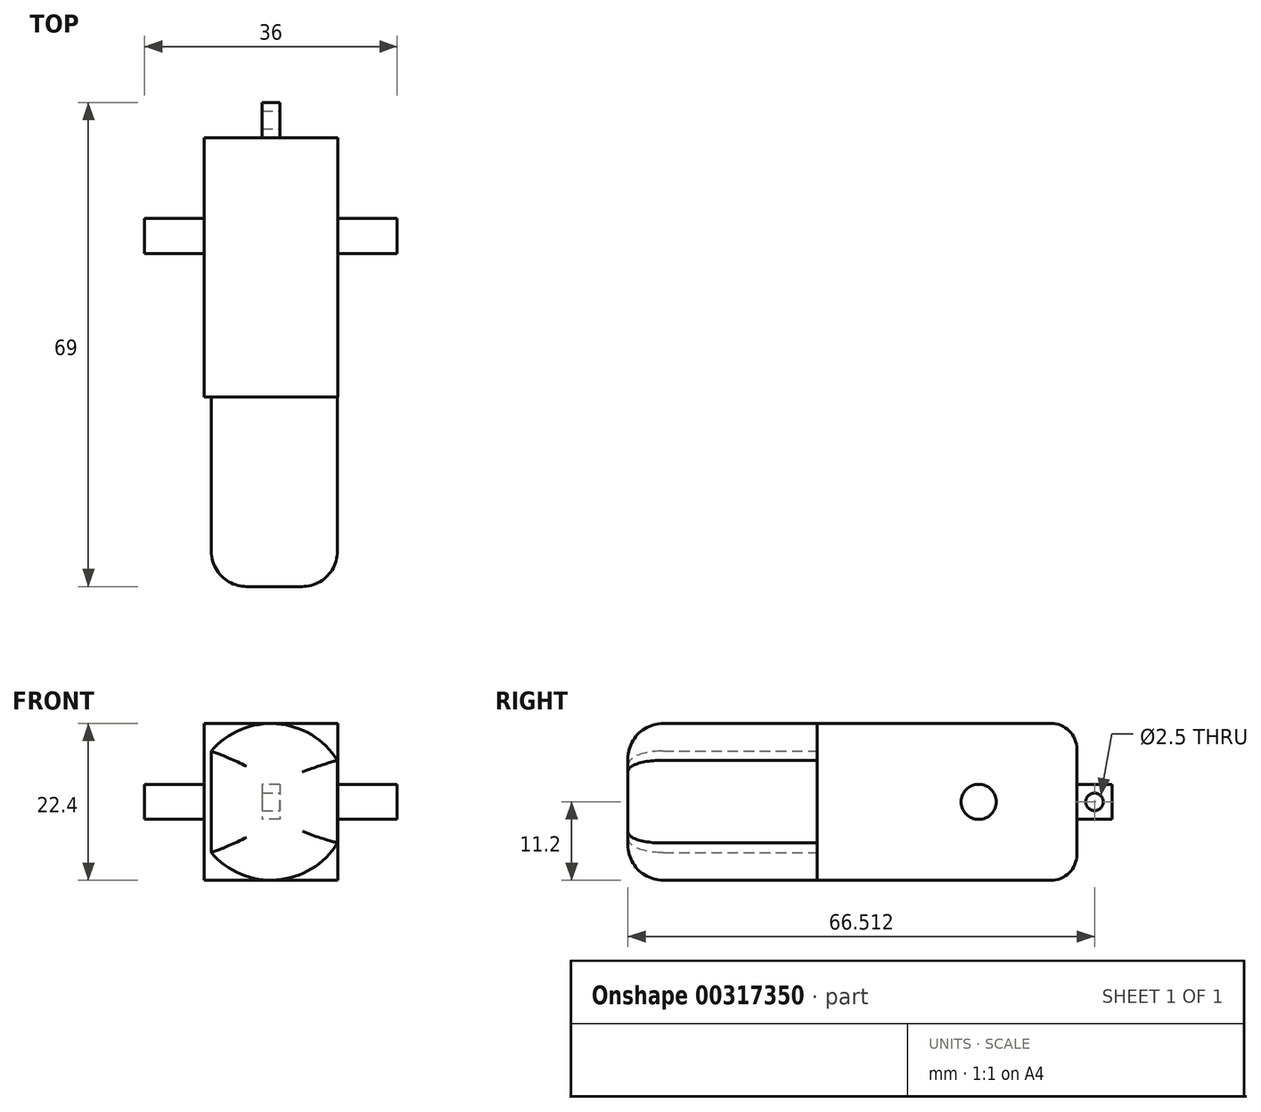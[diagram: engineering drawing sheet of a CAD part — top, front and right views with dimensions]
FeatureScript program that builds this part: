
annotation { "Feature Type Name" : "Feature", "Feature Type Description" : "" }
export const myFeature = defineFeature(function(context is Context, id is Id, definition is map)
    precondition{}
    {
        {
            var Q0;
            Q0=qCreatedBy(makeId("Right.planeOp"),FACE);
            var sketch = newSketch(context, id + "F0", { "sketchPlane" : qUnion([Q0])});
            skLineSegment(sketch, "E0.bottom", {"start": v(-18.5, 11.2) * mm, "end": v(18.5, 11.2) * mm});
            skLineSegment(sketch, "E0.top", {"start": v(-18.5, -11.2) * mm, "end": v(18.5, -11.2) * mm});
            skLineSegment(sketch, "E0.left", {"start": v(-18.5, 11.2) * mm, "end": v(-18.5, -11.2) * mm});
            skLineSegment(sketch, "E0.right", {"start": v(18.5, 11.2) * mm, "end": v(18.5, -11.2) * mm});
            skSolve(sketch);
        }
        {
            var Q0;
            Q0=qSketchRegion(id+"F0",true);
            extrude(context, id + "F1", {"entities" : qUnion([Q0]), "endBound" : BoundingType.SYMMETRIC, "depth" : 19 * mm});
        }
        {
            var Q0;
            Q0=makeQuery(id+"F1.opExtrude","SWEPT_EDGE",EDGE,{"disambiguationData":[OSD([sQuery(id+"F0.wireOp",EDGE,"E0.bottom"),sQuery(id+"F0.wireOp",EDGE,"E0.right")])]});
            var Q1;
            Q1=makeQuery(id+"F1.opExtrude","SWEPT_EDGE",EDGE,{"disambiguationData":[OSD([sQuery(id+"F0.wireOp",EDGE,"E0.top"),sQuery(id+"F0.wireOp",EDGE,"E0.right")])]});
            fillet(context, id + "F2", {"entities" : qUnion([Q0, Q1]), "radius" : 3.7 * mm, "tangentPropagation" : true, "allowEdgeOverflow" : false});
        }
        {
            var Q0;
            Q0=makeQuery(id+"F1.opExtrude","SWEPT_FACE",FACE,{"disambiguationData":[OSD([sQuery(id+"F0.wireOp",EDGE,"E0.right")])]});
            var sketch = newSketch(context, id + "F3", { "sketchPlane" : qUnion([Q0])});
            skLineSegment(sketch, "E1.bottom", {"start": v(-1.25, 2.5) * mm, "end": v(1.25, 2.5) * mm});
            skLineSegment(sketch, "E1.top", {"start": v(-1.25, -2.5) * mm, "end": v(1.25, -2.5) * mm});
            skLineSegment(sketch, "E1.left", {"start": v(-1.25, 2.5) * mm, "end": v(-1.25, -2.5) * mm});
            skLineSegment(sketch, "E1.right", {"start": v(1.25, 2.5) * mm, "end": v(1.25, -2.5) * mm});
            skSolve(sketch);
        }
        {
            var Q0;
            Q0=makeQuery(id+"F3.imprint","IMPRINT",FACE,{"disambiguationData":[TD([[makeQuery(id+"F3.imprint","IMPRINT",EDGE,{"derivedFrom":sQuery(id+"F3.wireOp",EDGE,"E1.bottom")}),-1.0]])]});
            extrude(context, id + "F4", {"entities" : qUnion([Q0]), "operationType" : NewBodyOperationType.ADD, "depth" : 5 * mm});
        }
        {
            var Q0;
            Q0=makeQuery(id+"F4.opExtrude","SWEPT_FACE",FACE,{"disambiguationData":[OSD([sQuery(id+"F3.wireOp",EDGE,"E1.left")])]});
            var sketch = newSketch(context, id + "F5", { "sketchPlane" : qUnion([Q0])});
            skCircle(sketch, "E2", {"center": v(21.01, 0) * mm, "radius": 1.25 * mm});
            skSolve(sketch);
        }
        {
            var Q0;
            Q0=makeQuery(id+"F5.imprint","IMPRINT",FACE,{"disambiguationData":[TD([[makeQuery(id+"F5.imprint","IMPRINT",EDGE,{"derivedFrom":sQuery(id+"F5.wireOp",EDGE,"E2")}),1.0]])]});
            extrude(context, id + "F6", {"entities" : qUnion([Q0]), "operationType" : NewBodyOperationType.REMOVE, "endBound" : BoundingType.THROUGH_ALL, "oppositeDirection" : true, "depth" : 25 * mm});
        }
        {
            var Q0;
            Q0=makeQuery(id+"F1.opExtrude","SWEPT_FACE",FACE,{"disambiguationData":[OSD([sQuery(id+"F0.wireOp",EDGE,"E0.left")])]});
            var sketch = newSketch(context, id + "F7", { "sketchPlane" : qUnion([Q0])});
            skLineSegment(sketch, "E3", {"start": v(-8.5, 7.24) * mm, "end": v(-8.5, -7.24) * mm});
            skArc(sketch, "E4", {"start": v(-8.5, -7.24) * mm, "mid": v(0.85, -11.13) * mm, "end": v(9.5, -5.87) * mm});
            skArc(sketch, "E5", {"start": v(9.46, 5.92) * mm, "mid": v(0.82, 11.13) * mm, "end": v(-8.5, 7.24) * mm});
            skLineSegment(sketch, "E6", {"start": v(9.46, 5.92) * mm, "end": v(9.5, -5.87) * mm});
            skSolve(sketch);
        }
        {
            var Q0;
            Q0=qSketchRegion(id+"F7",true);
            extrude(context, id + "F8", {"entities" : qUnion([Q0]), "operationType" : NewBodyOperationType.ADD, "depth" : 27 * mm});
        }
        {
            var Q0;
            Q0=makeQuery(id+"F8.opExtrude","CAP_FACE",FACE,{"disambiguationData":[OSD([sQuery(id+"F7.wireOp",EDGE,"E3"),sQuery(id+"F7.wireOp",EDGE,"E4"),sQuery(id+"F7.wireOp",EDGE,"E5"),sQuery(id+"F7.wireOp",EDGE,"E6")])],"isStart":false});
            fillet(context, id + "F9", {"entities" : qUnion([Q0]), "radius" : 5 * mm, "tangentPropagation" : true, "allowEdgeOverflow" : false});
        }
        {
            var Q0;
            Q0=makeQuery(id+"F1.opExtrude","CAP_FACE",FACE,{"disambiguationData":[OSD([sQuery(id+"F0.wireOp",EDGE,"E0.bottom"),sQuery(id+"F0.wireOp",EDGE,"E0.top"),sQuery(id+"F0.wireOp",EDGE,"E0.left"),sQuery(id+"F0.wireOp",EDGE,"E0.right")])],"isStart":false});
            var sketch = newSketch(context, id + "F10", { "sketchPlane" : qUnion([Q0])});
            skCircle(sketch, "E7", {"center": v(4.5, 0) * mm, "radius": 2.5 * mm});
            skLineSegment(sketch, "E8", {"start": v(7, 0) * mm, "end": v(18.5, 0) * mm, "construction": true});
            skSolve(sketch);
        }
        {
            var Q0;
            Q0=qSketchRegion(id+"F10",true);
            extrude(context, id + "F11", {"entities" : qUnion([Q0]), "depth" : 8.5 * mm});
        }
        {
            var Q0;
            Q0=makeQuery(id+"F11.opExtrude","SWEPT_BODY",BODY,{"disambiguationData":[OSD([sQuery(id+"F10.wireOp",EDGE,"E7")])]});
            var Q1;
            Q1=qCreatedBy(makeId("Right.planeOp"),FACE);
            mirror(context, id + "F12", {"operationType" : NewBodyOperationType.ADD, "entities" : qUnion([Q0]), "mirrorPlane" : qUnion([Q1])});
        }
    });
